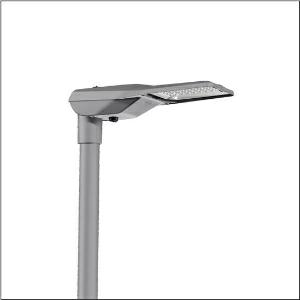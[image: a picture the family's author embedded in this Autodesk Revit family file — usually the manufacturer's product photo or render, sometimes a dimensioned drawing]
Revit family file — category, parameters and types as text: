
# Revit family: streetlight_sl_21_iq_mini___pl52_5xe2h31y08gb_067c
name_source: partatom
category: Lighting Fixtures
units: mm (PartAtom-declared; Revit-internal decimal feet)

## family parameters
Cut with Voids When Loaded = No
Host = Face
Light Source = No
Part Type = Normal
Room Calculation Point = No
Round Connector Dimension = Use Diameter
Shared = No

## types (1)
- --- (1 x LED, 5880 lm, 39.8 W, 3000K)
    Apparent Load = 40 VA
    CIE Flux Codes = 27 59 98 100 100
    Color Rendering = 70
    Color Temperature = 3000K
    Default Elevation = 1800 mm
    Description = Streetlight SL 21 iQ mini, mast luminaire, primary light control with lens, of PMMA, primary optical cover: cover, of toughened safety glass, transparent, light distribution: PL52, light emission: direct distribution, primary light characteristic: asymmetric, installation type: post-top, side-entry, LED, High Power LED, rated luminous flux: 5.880lm, luminous efficacy: 148lm/W, light colour: 730, colour temperature: 3000K, control gear: iQ-Street Remote, D4i with power reduction, control: pre-setting: logarithmic dimming characteristic, Street-Remote, Auto-Match, Temp-Guard, Lumen-Switch, Night-Set, Smart-Wire, Light-Fading, Desk-Remote (wireless, voltage-free reading and setting of iQ features in the workshop via application-optimized NFC function/RFID function), optimised constant luminous flux control (CLO 2.0), mains connection: 220..240V, AC, 50/60Hz, start of lifetime: 40W, end of service life: 41W, reduction: 18W, luminaire housing, of diecast aluminium, powder-coated, SITECO metallic grey (DB 702S), corrosivity category C5 high according to DIN EN ISO 12944, please order mast flange separately, inclination adjustable: 0°, 5°, 10°, 15°, sealing non-destructively replaceable, multi-level sealing system, length: 628mm, width: 235mm, height: 110mm, mast flange for spigot size: 42mm (side-entry): 5XC10008XM4, 60/48mm (side-entry/post-top): 5XC10108XM2, 76/60mm (side-entry/post-top): 5XC10108XM1, mounting height: 4..8m, Smart Interface below and above, protection rating (complete): IP66, insulation class (complete): insulation class II (safety insulation), certification: CE, ENEC, ENEC+, VDE, impact resistance: IK10, permissible operating ambient temperature for outdoor applications: -40..+50°C, standard-compliant lighting for roads and squares, packaging unit: 1 piece

Light Distribution: PL52
    Height = 110 mm
    Lamp = 1 x LED
    Lamp Light Flux = 5880 lm
    Lamp Power = 39.8 W
    Lamp count = 1
    Length = 625 mm
    Luminous efficacy = 148 lm/W
    Manufacturer = Siteco
    ModVariant = No
    Model = 5XE2H31Y08GB
    Mounting Place = Pole
    Mounting Type = Pole top
    Number of Poles = 1
    OnlyDefault = Yes
    Power Factor = 1
    Product Name = Streetlight SL 21 iQ mini | PL52
    Product group = mast luminaire | pylon top
    ProductGroupID = 6100
    Protection Class = Protection class II
    Protection Degree = IP 66
    RLX_Detail_Level = 1
    RLX_Emergency_Light_Flux = 0 lm
    RLX_Emergency_Type = 0
    RLX_Emergency_Type_DB = No
    RlxData = <blob elided: 102717 chars, md5=d3d77e60>
    Socket = socket
    Standby Power = 0 W
    System Light Flux = 5880 lm
    System Power = 40 W
    Type Comments = factory setting: luminous flux: 100 % | dim-lin: 254 | 800 mA
    Type Image = l_1003514.jpg
    URL = http://relux.com
    VarID = @adj_117629
    Voltage = 0 V
    Weight = 0.00 kg
    Width = 234 mm

## geometry (parser evidence)
native form markers: Blend x4, Sweep x9
no freeform markers — native parametric forms only
